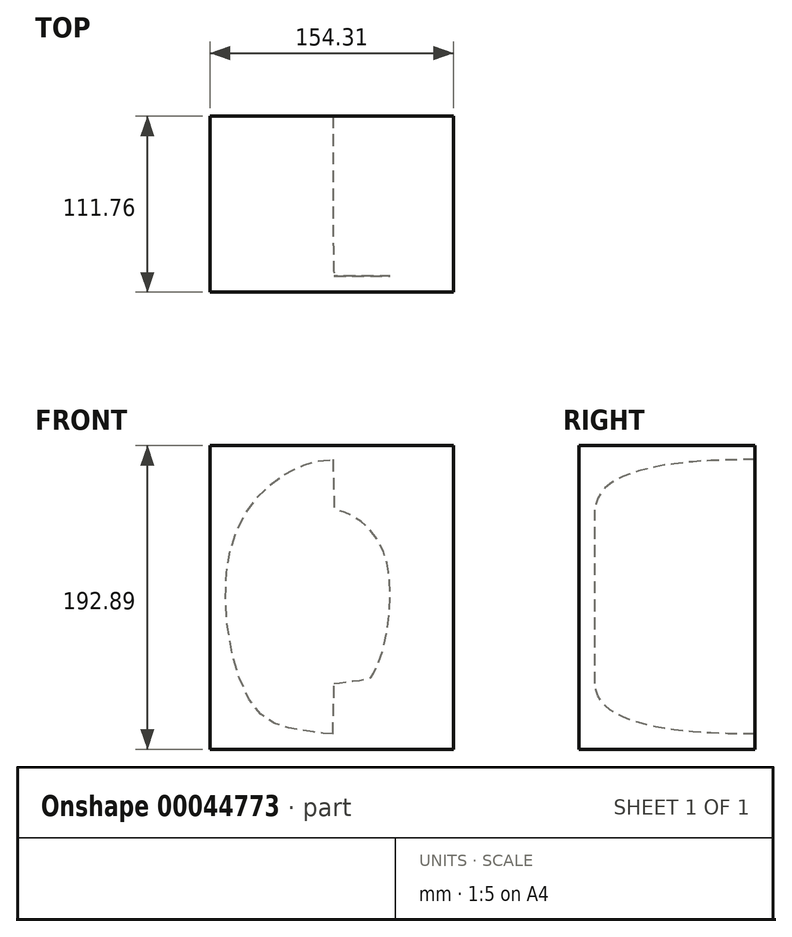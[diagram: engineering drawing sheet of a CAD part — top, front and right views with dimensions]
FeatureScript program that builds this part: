
annotation { "Feature Type Name" : "Feature", "Feature Type Description" : "" }
export const myFeature = defineFeature(function(context is Context, id is Id, definition is map)
    precondition{}
    {
        {
            var Q0;
            Q0=qCreatedBy(makeId("Front.planeOp"),FACE);
            var sketch = newSketch(context, id + "F0", { "sketchPlane" : qUnion([Q0])});
            skLineSegment(sketch, "E0.bottom", {"start": v(53.22, 97.1) * mm, "end": v(-101.1, 97.1) * mm});
            skLineSegment(sketch, "E0.top", {"start": v(53.22, -95.78) * mm, "end": v(-101.1, -95.78) * mm});
            skLineSegment(sketch, "E0.left", {"start": v(53.22, 97.1) * mm, "end": v(53.22, -95.78) * mm});
            skLineSegment(sketch, "E0.right", {"start": v(-101.1, 97.1) * mm, "end": v(-101.1, -95.78) * mm});
            skSolve(sketch);
        }
        {
            var Q0;
            Q0=qCreatedBy(makeId("Front.planeOp"),FACE);
            var sketch = newSketch(context, id + "F1", { "sketchPlane" : qUnion([Q0])});
            skFitSpline(sketch, "E1", {"points": [v(-23.21, -86.03) * mm, v(-6.89, -84.16) * mm, v(24.46, -71.68) * mm, v(43.38, 23.79) * mm, v(15.43, 73.24) * mm, v(-8.65, 86.15) * mm, v(-23.21, 88.18) * mm], "startDerivative": vector(150.8, -3.72) * mm, "endDerivative": vector(-150.03, 4.25) * mm});
            skFitSpline(sketch, "E2.MirrorCS", {"points": [v(-23.21, -86.03) * mm, v(-39.53, -84.16) * mm, v(-70.88, -71.68) * mm, v(-89.8, 23.79) * mm, v(-61.85, 73.24) * mm, v(-37.77, 86.15) * mm, v(-23.21, 88.18) * mm], "startDerivative": vector(-150.8, -3.72) * mm, "endDerivative": vector(150.03, 4.25) * mm});
            skSolve(sketch);
        }
        {
            var Q0;
            Q0=makeQuery(id+"F0.imprint","IMPRINT",FACE,{"disambiguationData":[TD([[makeQuery(id+"F0.imprint","IMPRINT",EDGE,{"derivedFrom":sQuery(id+"F0.wireOp",EDGE,"E0.bottom")}),1.0]])]});
            extrude(context, id + "F2", {"entities" : qUnion([Q0]), "depth" : 111.76 * mm});
        }
        {
            var Q0;
            Q0=makeQuery(id+"F1.imprint","IMPRINT",FACE,{"disambiguationData":[TD([[makeQuery(id+"F1.imprint","IMPRINT",EDGE,{"derivedFrom":sQuery(id+"F1.wireOp",EDGE,"E1")}),1.0]])]});
            cPlane(context, id + "F3", {"entities" : qUnion([Q0]), "cplaneType" : CPlaneType.OFFSET, "offset" : 101.6 * mm, "width" : 152.4 * mm, "height" : 152.4 * mm});
        }
        {
            var Q0;
            Q0=qCreatedBy(id+"F3.planeOp",FACE);
            var sketch = newSketch(context, id + "F4", { "sketchPlane" : qUnion([Q0])});
            skFitSpline(sketch, "E3.0", {"points": [v(-20.73, 56.23) * mm, v(-21.35, 56.2) * mm, v(-22.44, 56.17) * mm, v(-23.7, 56.1) * mm, v(-24.62, 56) * mm, v(-25.32, 55.9) * mm, v(-25.93, 55.8) * mm, v(-26.48, 55.67) * mm, v(-27, 55.53) * mm, v(-27.47, 55.4) * mm, v(-27.97, 55.24) * mm, v(-28.7, 55) * mm, v(-29.7, 54.62) * mm, v(-31.46, 53.87) * mm, v(-33.41, 52.9) * mm, v(-35.47, 51.72) * mm, v(-37.05, 50.7) * mm, v(-38.65, 49.58) * mm, v(-40.27, 48.34) * mm, v(-41.87, 46.98) * mm, v(-43.96, 45.03) * mm, v(-46.47, 42.32) * mm, v(-49.26, 38.56) * mm, v(-51.8, 34.2) * mm, v(-53.67, 29.94) * mm, v(-54.97, 26.06) * mm, v(-55.7, 23.4) * mm, v(-56.2, 21.15) * mm, v(-56.56, 19.37) * mm, v(-56.87, 17.53) * mm, v(-57.15, 15.55) * mm, v(-57.39, 13.48) * mm, v(-57.65, 10.58) * mm, v(-57.87, 6.75) * mm, v(-57.95, 1.9) * mm, v(-57.8, -4.8) * mm, v(-57.12, -13.42) * mm, v(-55.56, -23.6) * mm, v(-53.73, -31.44) * mm, v(-52.04, -37.04) * mm, v(-50.7, -40.81) * mm, v(-49.33, -44.07) * mm, v(-48.22, -46.29) * mm, v(-47.42, -47.7) * mm, v(-46.87, -48.59) * mm, v(-46.4, -49.27) * mm, v(-46.1, -49.67) * mm, v(-45.92, -49.89) * mm, v(-45.82, -50) * mm, v(-45.77, -50.06) * mm, v(-45.73, -50.1) * mm, v(-45.7, -50.13) * mm, v(-45.66, -50.16) * mm, v(-45.62, -50.2) * mm, v(-45.57, -50.23) * mm, v(-45.36, -50.35) * mm, v(-44.86, -50.57) * mm, v(-44, -50.85) * mm, v(-42.7, -51.17) * mm, v(-41.29, -51.44) * mm, v(-39.94, -51.65) * mm, v(-38.81, -51.81) * mm, v(-37.58, -51.98) * mm, v(-36.45, -52.12) * mm, v(-35.48, -52.25) * mm, v(-34.72, -52.35) * mm, v(-33.92, -52.45) * mm, v(-33.08, -52.57) * mm, v(-32.28, -52.69) * mm, v(-31.25, -52.84) * mm, v(-30.05, -53.03) * mm, v(-28.73, -53.24) * mm, v(-27.56, -53.43) * mm, v(-26.52, -53.6) * mm, v(-25.33, -53.79) * mm, v(-24.19, -53.95) * mm, v(-23.3, -54.04) * mm, v(-22.79, -54.07) * mm, v(-22.55, -54.08) * mm, v(-22.42, -54.07) * mm]});
            skFitSpline(sketch, "E3.1", {"points": [v(-22.42, -54.07) * mm, v(-22.3, -54.08) * mm, v(-22.06, -54.07) * mm, v(-21.54, -54.04) * mm, v(-20.65, -53.95) * mm, v(-19.51, -53.79) * mm, v(-18.32, -53.6) * mm, v(-17.29, -53.43) * mm, v(-16.11, -53.24) * mm, v(-14.8, -53.03) * mm, v(-13.6, -52.84) * mm, v(-12.57, -52.69) * mm, v(-11.77, -52.57) * mm, v(-10.93, -52.45) * mm, v(-10.13, -52.35) * mm, v(-9.37, -52.25) * mm, v(-8.4, -52.12) * mm, v(-7.27, -51.98) * mm, v(-6.03, -51.81) * mm, v(-4.9, -51.65) * mm, v(-3.55, -51.44) * mm, v(-2.13, -51.17) * mm, v(-0.85, -50.85) * mm, v(0.02, -50.57) * mm, v(0.51, -50.35) * mm, v(0.72, -50.23) * mm, v(0.77, -50.2) * mm, v(0.81, -50.16) * mm, v(0.85, -50.13) * mm, v(0.88, -50.1) * mm, v(0.93, -50.06) * mm, v(0.98, -50) * mm, v(1.08, -49.89) * mm, v(1.25, -49.67) * mm, v(1.56, -49.27) * mm, v(2.03, -48.59) * mm, v(2.58, -47.7) * mm, v(3.38, -46.29) * mm, v(4.48, -44.07) * mm, v(5.85, -40.81) * mm, v(7.2, -37.04) * mm, v(8.9, -31.44) * mm, v(10.72, -23.6) * mm, v(12.27, -13.42) * mm, v(12.95, -4.8) * mm, v(13.1, 1.9) * mm, v(13.03, 6.75) * mm, v(12.8, 10.58) * mm, v(12.54, 13.48) * mm, v(12.3, 15.55) * mm, v(12.03, 17.53) * mm, v(11.72, 19.37) * mm, v(11.37, 21.15) * mm, v(10.85, 23.4) * mm, v(10.13, 26.06) * mm, v(8.83, 29.94) * mm, v(6.96, 34.2) * mm, v(4.41, 38.56) * mm, v(1.62, 42.32) * mm, v(-0.88, 45.03) * mm, v(-2.97, 46.98) * mm, v(-4.58, 48.34) * mm, v(-6.2, 49.58) * mm, v(-7.8, 50.7) * mm, v(-9.37, 51.72) * mm, v(-11.43, 52.9) * mm, v(-13.38, 53.87) * mm, v(-15.14, 54.62) * mm, v(-16.14, 55) * mm, v(-16.87, 55.24) * mm, v(-17.38, 55.4) * mm, v(-17.83, 55.53) * mm, v(-18.36, 55.67) * mm, v(-18.92, 55.8) * mm, v(-19.52, 55.9) * mm, v(-20.23, 56) * mm, v(-21.15, 56.1) * mm, v(-22.4, 56.17) * mm, v(-23.5, 56.2) * mm, v(-24.11, 56.23) * mm]});
            skSolve(sketch);
        }
        {
            var Q1;
            Q1=makeQuery(id+"F1.imprint","IMPRINT",FACE,{"disambiguationData":[TD([[makeQuery(id+"F1.imprint","IMPRINT",EDGE,{"derivedFrom":sQuery(id+"F1.wireOp",EDGE,"E1")}),1.0]])]});
            var Q2;
            Q2=makeQuery(id+"F4.imprint","IMPRINT",FACE,{"disambiguationData":[TD([[makeQuery(id+"F4.imprint","IMPRINT",EDGE,{"derivedFrom":sQuery(id+"F4.wireOp",EDGE,"E3.0")}),1.0]])]});
            loft(context, id + "F5", {"operationType" : NewBodyOperationType.REMOVE, "startCondition" : LoftEndDerivativeType.NORMAL_TO_PROFILE, "startMagnitude" : .75, "endCondition" : LoftEndDerivativeType.TANGENT_TO_PROFILE, "endMagnitude" : 3, "sheetProfilesArray" : [{ "sheetProfileEntities" : qUnion([Q1]) }, { "sheetProfileEntities" : qUnion([Q2]) }]});
        }
    });
